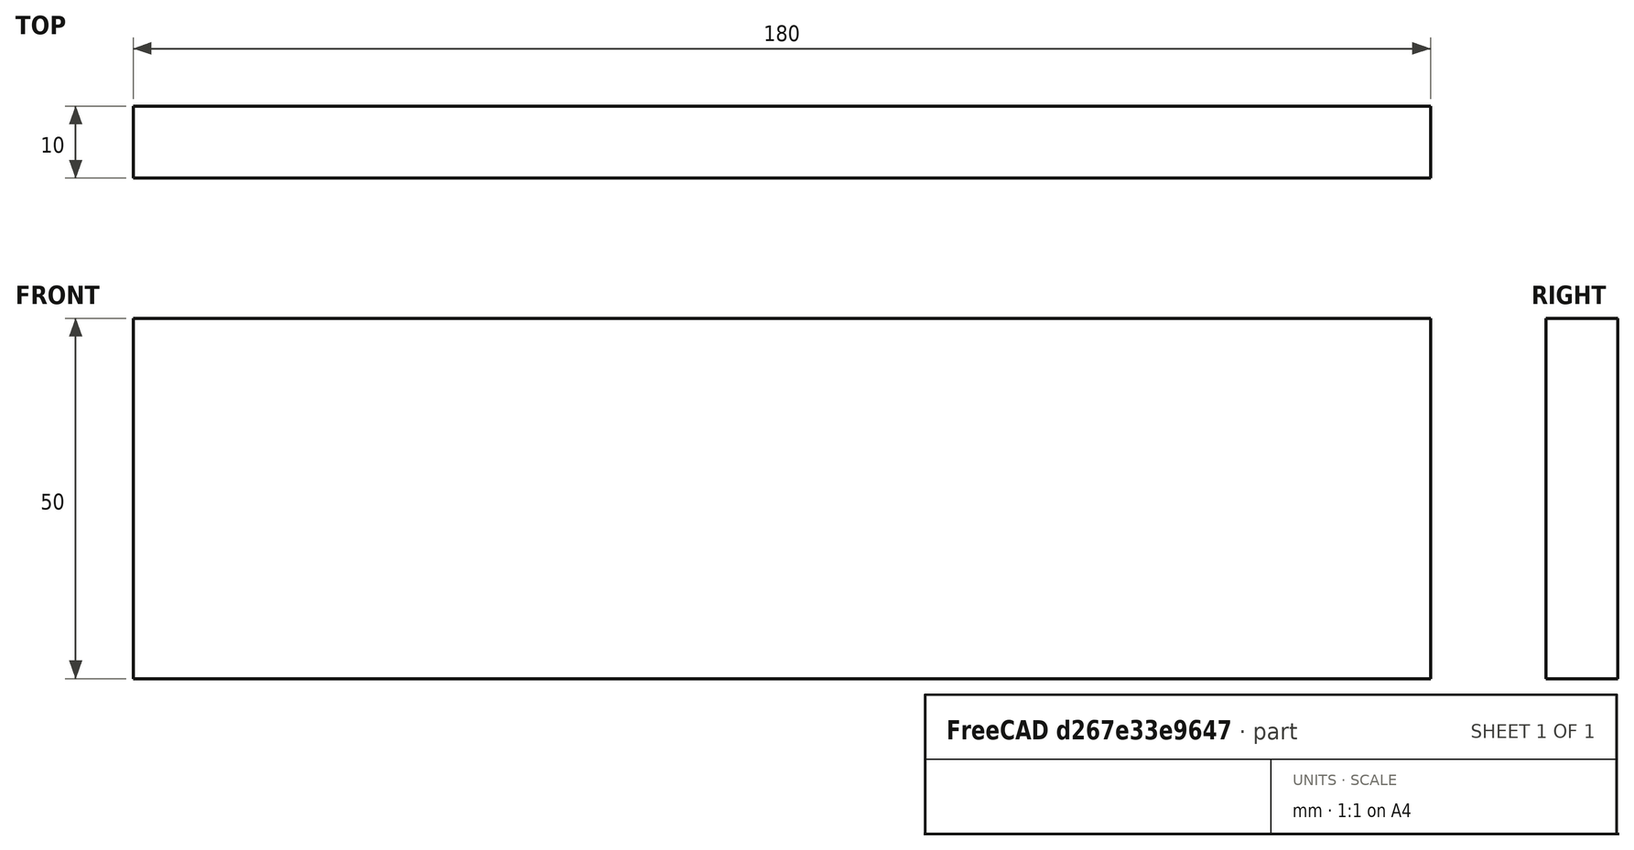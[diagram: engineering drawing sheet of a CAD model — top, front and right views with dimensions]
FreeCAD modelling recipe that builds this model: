
FCSTD DOCUMENT  (FreeCAD 0.15R4671 (Git))
Label: Flat Bar 180x10 EN10058 S235JR
License: All rights reserved
LicenseURL: http://en.wikipedia.org/wiki/All_rights_reserved
objects: Sketcher::SketchObject×1, Part::Extrusion×1
note: 2 computed .brp shape members not serialized (recipe doc carries the construction recipe); baked Part::Feature solids carry a one-line shape summary decoded from their .brp

FEATURE [Sketcher::SketchObject] Sketch
  sketch-geometry (4):
    g0: LineSegment StartX=-90 StartY=-5 StartZ=0 EndX=90 EndY=-5 EndZ=0
    g1: LineSegment StartX=90 StartY=-5 StartZ=0 EndX=90 EndY=5 EndZ=0
    g2: LineSegment StartX=90 StartY=5 StartZ=0 EndX=-90 EndY=5 EndZ=0
    g3: LineSegment StartX=-90 StartY=5 StartZ=0 EndX=-90 EndY=-5 EndZ=0
  constraints (12):
    c: Coincident(g0,g1)
    c: Coincident(g1,g2)
    c: Coincident(g2,g3)
    c: Coincident(g3,g0)
    c: Horizontal(g0)
    c: Horizontal(g2)
    c: Vertical(g1)
    c: Vertical(g3)
    c: Symmetric(g1,g2,g-2)
    c: Symmetric(g0,g1,g-1)
    c: DistanceY(g1) = 10
    c: DistanceX(g0) = 180
FEATURE [Part::Extrusion] Extrude  label="Flat Bar 180x10 EN10058 S235JR"
  Base = -> Sketch
  Dir = (0,0,50)
  Solid = true
